# Revit family: レンジフードファン(ブース形同時給排気タイプ)_60Hz
name_source: partatom
category: 機械設備
units: mm (PartAtom-declared; Revit-internal decimal feet)

## family parameters
OmniClass タイトル = Heat Exchangers for Ventilation Air
OmniClass 番号 = 23.75.10.34.21
パーツ タイプ = 標準
ロード時にボイドで切り取り = いいえ
丸型コネクタ寸法 = 直径を使用
作業面ベース = いいえ
共有 = いいえ
常に垂直 = はい
部屋計算ポイント = いいえ

## types (2) — shared parameters
D1 = 469
D2 = 405
D3 = 55  [stored 0.180446 ft]
Depth = 650  [stored 2.13255 ft]
Duct_D = 135  [stored 0.442913 ft]
Duct_EA_W = 167  [stored 0.5479 ft]
Duct_H = 91
Duct_Height = 55  [stored 0.180446 ft]
Duct_SA_W = 109  [stored 0.357612 ft]
Duct_Shutter_Depth = 182  [stored 0.597113 ft]
Duct_Shutter_Height = 182  [stored 0.597113 ft]
Duct_Shutter_Width = 182  [stored 0.597113 ft]
EAサイズ_D = 148  [stored 0.485564 ft]
EAダクト接続口_上部 = はい
EAダクト接続口_後部 = いいえ
H1 = 129  [stored 0.423228 ft]
H2 = 600  [stored 1.9685 ft]
Height = 400  [stored 1.31234 ft]
IfcExportAs = IfcFanType
IfcExportType = CENTRIFUGALFORWARDCURVED
MAX静圧 = 0.0 Pa
MID静圧 = 0.0 Pa
MIN静圧 = 0.0 Pa
OmniClassCode = 23-33 31 19 13 15
SAサイズ_D = 148  [stored 0.485564 ft]
SAダクト接続口_上部 = はい
SAダクト接続口_後部 = いいえ
URL = https://www.mitsubishielectric.co.jp
Uniclass2015Code = Pr_65_67_29_12
Uniclass2015Title = Centrifugal fans
Uniclass2015Version = Systems v1.9
W1 = 300  [stored 0.984252 ft]
Width = 600  [stored 1.9685 ft]
☑給気／□排気 = いいえ
ダクト径 = 150 mm
マテリアル = 鋼板(シルバー)
仕様書バージョン = Version1.0
企業コード = 108420
分類コード = 50052503100060
周波数 = 60 Hz
呼称 = 遠心送風機
外気量 = 0.0 m³/h
天吊用穴_D = 280  [stored 0.918635 ft]
天吊用穴_Height = 120  [stored 0.393701 ft]
天吊用穴_ピッチ1 = 238  [stored 0.78084 ft]
天吊用穴_ピッチ2 = 221  [stored 0.725066 ft]
天吊用穴_径 = 25  [stored 0.082021 ft]
実風量 = 0.0 m³/h
形式 = 片吸込形
排気量 = 0.0 m³/h
極数 = 2
機外静圧 = 0.0 Pa
機外静圧_排気 = 210.0 Pa
法定耐用年数 = 15
相 = 1
積算_科目 = 2 換気設備
符号 = FE
製品リリース年月 = 2022年6月1日
製品出荷対象 = 国内
製造元 = 三菱電機株式会社
設置方法 = 天吊
設計風量 = 0.0 m³/h
説明 = レンジフードファン 深形 強制給排気タイプ
負荷分類 = 3_ファン類
運転質量 = 0.00 kg
電動機出力 = 0 W
電圧 = 100 V
zero-valued in all types: Clearance Back, Clearance Bottom, Clearance Front, Clearance Left, Clearance Right, Clearance Top

## per-type parameters (varying)
| type | MAX風量 | MID風量 | MIN風量 | 価格 | 消費電力 | 製品質量 | 質量 | 風量 | 騒音レベル(dB(A)) |
| V-604KQH8 | 585.0 m³/h | 320.0 m³/h | 190.0 m³/h | 208700 $ | 198 W | 30.00 kg | 36.00 kg | 585.0 m³/h | 49 |
| V-604KCQ8 | 630.0 m³/h | 345.0 m³/h | 245.0 m³/h | 178900 $ | 195 W | 26.00 kg | 31.20 kg | 630.0 m³/h | 48.5 |

note: column(s) folded — value = type name in every type: モデル

note: [stored X ft] marks values corroborated as IEEE doubles in the binary element streams (Revit-internal decimal feet)

## geometry (parser evidence)
native form markers: Blend x2
no freeform markers — native parametric forms only
